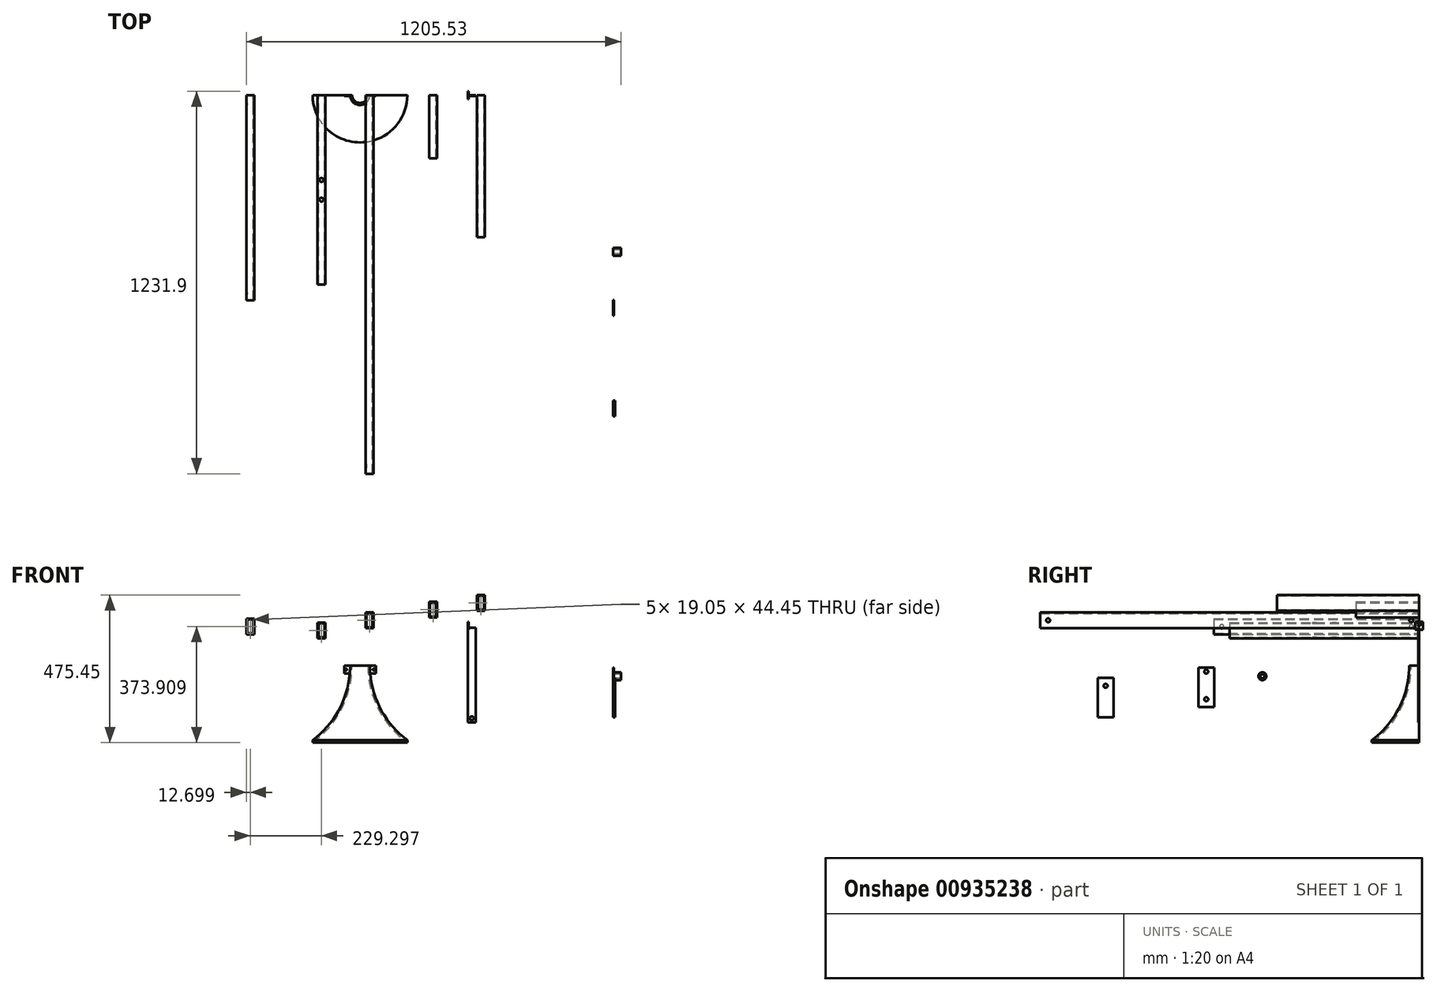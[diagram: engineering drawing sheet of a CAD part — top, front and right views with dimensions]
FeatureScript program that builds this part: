
annotation { "Feature Type Name" : "Feature", "Feature Type Description" : "" }
export const myFeature = defineFeature(function(context is Context, id is Id, definition is map)
    precondition{}
    {
        {
            var Q0;
            Q0=qCreatedBy(makeId("Front.planeOp"),FACE);
            var sketch = newSketch(context, id + "F0", { "sketchPlane" : qUnion([Q0])});
            skLineSegment(sketch, "E0.bottom", {"start": v(-947.66, 282.46) * mm, "end": v(-928.6, 282.46) * mm});
            skLineSegment(sketch, "E0.top", {"start": v(-947.66, 238) * mm, "end": v(-928.6, 238) * mm});
            skLineSegment(sketch, "E0.left", {"start": v(-947.66, 282.46) * mm, "end": v(-947.66, 238) * mm});
            skLineSegment(sketch, "E0.right", {"start": v(-928.6, 282.46) * mm, "end": v(-928.6, 238) * mm});
            skLineSegment(sketch, "E1.0", {"start": v(-950.83, 285.63) * mm, "end": v(-950.83, 234.83) * mm});
            skLineSegment(sketch, "E1.1", {"start": v(-950.83, 285.63) * mm, "end": v(-925.43, 285.63) * mm});
            skLineSegment(sketch, "E1.2", {"start": v(-925.43, 285.63) * mm, "end": v(-925.43, 234.83) * mm});
            skLineSegment(sketch, "E1.3", {"start": v(-950.83, 234.83) * mm, "end": v(-925.43, 234.83) * mm});
            skSolve(sketch);
        }
        {
            var Q0;
            Q0 = qSketchRegion(id + "F0", true);
            extrude(context, id + "F1", {"entities" : qUnion([Q0]), "depth" : 609.6 * mm, "offsetDistance" : 25.4 * mm});
        }
        {
            var Q0;
            Q0=qCreatedBy(makeId("Front.planeOp"),FACE);
            var sketch = newSketch(context, id + "F2", { "sketchPlane" : qUnion([Q0])});
            skLineSegment(sketch, "E2.bottom", {"start": v(-1176.96, 295.25) * mm, "end": v(-1157.9, 295.25) * mm});
            skLineSegment(sketch, "E2.top", {"start": v(-1176.96, 250.8) * mm, "end": v(-1157.9, 250.8) * mm});
            skLineSegment(sketch, "E2.left", {"start": v(-1176.96, 295.25) * mm, "end": v(-1176.96, 250.8) * mm});
            skLineSegment(sketch, "E2.right", {"start": v(-1157.9, 295.25) * mm, "end": v(-1157.9, 250.8) * mm});
            skLineSegment(sketch, "E3.0", {"start": v(-1180.13, 298.43) * mm, "end": v(-1180.13, 247.63) * mm});
            skLineSegment(sketch, "E3.1", {"start": v(-1180.13, 298.43) * mm, "end": v(-1154.73, 298.43) * mm});
            skLineSegment(sketch, "E3.2", {"start": v(-1154.73, 298.43) * mm, "end": v(-1154.73, 247.63) * mm});
            skLineSegment(sketch, "E3.3", {"start": v(-1180.13, 247.63) * mm, "end": v(-1154.73, 247.63) * mm});
            skSolve(sketch);
        }
        {
            var Q0;
            Q0=makeQuery(id+"F2.imprint","IMPRINT",FACE,{"disambiguationData":[TD([[makeQuery(id+"F2.imprint","IMPRINT",EDGE,{"derivedFrom":sQuery(id+"F2.wireOp",EDGE,"E2.bottom")}),1.0]])]});
            var Q1;
            Q1 = qConstructionFilter(qBodyType(qCreatedBy(id + "F2" ,EDGE), BodyType.WIRE), ConstructionObject.NO);
            extrude(context, id + "F3", {"entities" : qUnion([Q0]), "surfaceEntities" : qUnion([Q1]), "depth" : 660.4 * mm, "offsetDistance" : 25.4 * mm});
        }
        {
            var Q0;
            Q0=qCreatedBy(makeId("Front.planeOp"),FACE);
            var sketch = newSketch(context, id + "F4", { "sketchPlane" : qUnion([Q0])});
            skLineSegment(sketch, "E4.bottom", {"start": v(-792.92, 315.07) * mm, "end": v(-773.87, 315.07) * mm});
            skLineSegment(sketch, "E4.top", {"start": v(-792.92, 270.62) * mm, "end": v(-773.87, 270.62) * mm});
            skLineSegment(sketch, "E4.left", {"start": v(-792.92, 315.07) * mm, "end": v(-792.92, 270.62) * mm});
            skLineSegment(sketch, "E4.right", {"start": v(-773.87, 315.07) * mm, "end": v(-773.87, 270.62) * mm});
            skLineSegment(sketch, "E5.0", {"start": v(-796.1, 318.24) * mm, "end": v(-796.1, 267.44) * mm});
            skLineSegment(sketch, "E5.1", {"start": v(-796.1, 318.24) * mm, "end": v(-770.7, 318.24) * mm});
            skLineSegment(sketch, "E5.2", {"start": v(-770.7, 318.24) * mm, "end": v(-770.7, 267.44) * mm});
            skLineSegment(sketch, "E5.3", {"start": v(-796.1, 267.44) * mm, "end": v(-770.7, 267.44) * mm});
            skSolve(sketch);
        }
        {
            var Q0;
            Q0 = qSketchRegion(id + "F4", true);
            extrude(context, id + "F5", {"entities" : qUnion([Q0]), "depth" : 1219.2 * mm, "offsetDistance" : 25.4 * mm});
        }
        {
            var Q0;
            Q0=makeQuery(id+"F5.opExtrude","SWEPT_FACE",FACE,{"disambiguationData":[OSD([sQuery(id+"F4.wireOp",EDGE,"E5.2")])]});
            var sketch = newSketch(context, id + "F6", { "sketchPlane" : qUnion([Q0])});
            skCircle(sketch, "E6", {"center": v(-1193.8, 292.84) * mm, "radius": 6.35 * mm});
            skPoint(sketch, "E6.centerSnap0", {"position": v(-1219.2, 292.84) * mm});
            skCircle(sketch, "E7", {"center": v(-25.4, 292.84) * mm, "radius": 6.35 * mm});
            skPoint(sketch, "E7.centerSnap0", {"position": v(0, 292.84) * mm});
            skSolve(sketch);
        }
        {
            var Q0;
            Q0 = qSketchRegion(id + "F6", true);
            extrude(context, id + "F7", {"entities" : qUnion([Q0]), "operationType" : NewBodyOperationType.REMOVE, "oppositeDirection" : true, "depth" : 50.8 * mm, "offsetDistance" : 25.4 * mm});
        }
        {
            var Q0;
            Q0=qCreatedBy(makeId("Right.planeOp"),FACE);
            var sketch = newSketch(context, id + "F8", { "sketchPlane" : qUnion([Q0])});
            skLineSegment(sketch, "E8.bottom", {"start": v(-1034.2, 107.22) * mm, "end": v(-983.4, 107.22) * mm});
            skLineSegment(sketch, "E8.top", {"start": v(-1034.2, -19.78) * mm, "end": v(-983.4, -19.78) * mm});
            skLineSegment(sketch, "E8.left", {"start": v(-1034.2, 107.22) * mm, "end": v(-1034.2, -19.78) * mm});
            skLineSegment(sketch, "E8.right", {"start": v(-983.4, 107.22) * mm, "end": v(-983.4, -19.78) * mm});
            skCircle(sketch, "E9", {"center": v(-1008.8, 81.82) * mm, "radius": 6.35 * mm});
            skPoint(sketch, "E9.centerSnap0", {"position": v(-1008.8, 107.22) * mm});
            skSolve(sketch);
        }
        {
            var Q0;
            Q0=makeQuery(id+"F8.imprint","IMPRINT",FACE,{"disambiguationData":[TD([[makeQuery(id+"F8.imprint","IMPRINT",EDGE,{"derivedFrom":sQuery(id+"F8.wireOp",EDGE,"E8.bottom")}),-1.0]])]});
            extrude(context, id + "F9", {"entities" : qUnion([Q0]), "depth" : 6.35 * mm, "offsetDistance" : 25.4 * mm});
        }
        {
            var Q0;
            Q0=makeQuery(id+"F1.opExtrude","SWEPT_FACE",FACE,{"disambiguationData":[OSD([sQuery(id+"F0.wireOp",EDGE,"E1.1")])]});
            var sketch = newSketch(context, id + "F10", { "sketchPlane" : qUnion([Q0])});
            skCircle(sketch, "E10", {"center": v(-938.13, -273.05) * mm, "radius": 6.35 * mm});
            skPoint(sketch, "E10.centerSnap0", {"position": v(-938.13, 0) * mm});
            skCircle(sketch, "E11", {"center": v(-938.13, -336.55) * mm, "radius": 6.35 * mm});
            skSolve(sketch);
        }
        {
            var Q0;
            Q0 = qSketchRegion(id + "F10", true);
            extrude(context, id + "F11", {"entities" : qUnion([Q0]), "operationType" : NewBodyOperationType.REMOVE, "oppositeDirection" : true, "depth" : 50.8 * mm, "offsetDistance" : 25.4 * mm});
        }
        {
            var Q0;
            Q0=qCreatedBy(makeId("Front.planeOp"),FACE);
            var sketch = newSketch(context, id + "F12", { "sketchPlane" : qUnion([Q0])});
            skLineSegment(sketch, "E12.bottom", {"start": v(-588.77, 349) * mm, "end": v(-569.72, 349) * mm});
            skLineSegment(sketch, "E12.top", {"start": v(-588.77, 304.56) * mm, "end": v(-569.72, 304.56) * mm});
            skLineSegment(sketch, "E12.left", {"start": v(-588.77, 349) * mm, "end": v(-588.77, 304.56) * mm});
            skLineSegment(sketch, "E12.right", {"start": v(-569.72, 349) * mm, "end": v(-569.72, 304.56) * mm});
            skLineSegment(sketch, "E13.0", {"start": v(-591.95, 352.18) * mm, "end": v(-591.95, 301.38) * mm});
            skLineSegment(sketch, "E13.1", {"start": v(-591.95, 352.18) * mm, "end": v(-566.55, 352.18) * mm});
            skLineSegment(sketch, "E13.2", {"start": v(-566.55, 352.18) * mm, "end": v(-566.55, 301.38) * mm});
            skLineSegment(sketch, "E13.3", {"start": v(-591.95, 301.38) * mm, "end": v(-566.55, 301.38) * mm});
            skSolve(sketch);
        }
        {
            var Q0;
            Q0=makeQuery(id+"F12.imprint","IMPRINT",FACE,{"disambiguationData":[TD([[makeQuery(id+"F12.imprint","IMPRINT",EDGE,{"derivedFrom":sQuery(id+"F12.wireOp",EDGE,"E12.bottom")}),1.0]])]});
            var Q1;
            Q1 = qConstructionFilter(qBodyType(qCreatedBy(id + "F12" ,EDGE), BodyType.WIRE), ConstructionObject.NO);
            extrude(context, id + "F13", {"entities" : qUnion([Q0]), "surfaceEntities" : qUnion([Q1]), "depth" : 203.2 * mm, "offsetDistance" : 25.4 * mm});
        }
        {
            var Q0;
            Q0=qCreatedBy(makeId("Front.planeOp"),FACE);
            var sketch = newSketch(context, id + "F14", { "sketchPlane" : qUnion([Q0])});
            skLineSegment(sketch, "E14.bottom", {"start": v(-434.38, 371.4) * mm, "end": v(-415.33, 371.4) * mm});
            skLineSegment(sketch, "E14.top", {"start": v(-434.38, 326.95) * mm, "end": v(-415.33, 326.95) * mm});
            skLineSegment(sketch, "E14.left", {"start": v(-434.38, 371.4) * mm, "end": v(-434.38, 326.95) * mm});
            skLineSegment(sketch, "E14.right", {"start": v(-415.33, 371.4) * mm, "end": v(-415.33, 326.95) * mm});
            skLineSegment(sketch, "E15.0", {"start": v(-437.55, 374.57) * mm, "end": v(-437.55, 323.77) * mm});
            skLineSegment(sketch, "E15.1", {"start": v(-437.55, 374.57) * mm, "end": v(-412.15, 374.57) * mm});
            skLineSegment(sketch, "E15.2", {"start": v(-412.15, 374.57) * mm, "end": v(-412.15, 323.77) * mm});
            skLineSegment(sketch, "E15.3", {"start": v(-437.55, 323.77) * mm, "end": v(-412.15, 323.77) * mm});
            skSolve(sketch);
        }
        {
            var Q0;
            Q0=makeQuery(id+"F14.imprint","IMPRINT",FACE,{"disambiguationData":[TD([[makeQuery(id+"F14.imprint","IMPRINT",EDGE,{"derivedFrom":sQuery(id+"F14.wireOp",EDGE,"E14.bottom")}),1.0]])]});
            var Q1;
            Q1 = qConstructionFilter(qBodyType(qCreatedBy(id + "F14" ,EDGE), BodyType.WIRE), ConstructionObject.NO);
            extrude(context, id + "F15", {"entities" : qUnion([Q0]), "surfaceEntities" : qUnion([Q1]), "depth" : 457.2 * mm, "offsetDistance" : 25.4 * mm});
        }
        {
            var Q0;
            Q0=makeQuery(id+"F3.opExtrude","SWEPT_FACE",FACE,{"disambiguationData":[OSD([sQuery(id+"F2.wireOp",EDGE,"E3.0")])]});
            var sketch = newSketch(context, id + "F16", { "sketchPlane" : qUnion([Q0])});
            skCircle(sketch, "E16", {"center": v(635, 273.03) * mm, "radius": 6.35 * mm});
            skPoint(sketch, "E16.centerSnap0", {"position": v(660.4, 273.03) * mm});
            skCircle(sketch, "E17", {"center": v(25.4, 273.03) * mm, "radius": 6.35 * mm});
            skPoint(sketch, "E17.centerSnap0", {"position": v(0, 273.03) * mm});
            skSolve(sketch);
        }
        {
            var Q0;
            Q0 = qSketchRegion(id + "F16", true);
            extrude(context, id + "F17", {"entities" : qUnion([Q0]), "operationType" : NewBodyOperationType.REMOVE, "oppositeDirection" : true, "depth" : 38.1 * mm, "offsetDistance" : 25.4 * mm});
        }
        {
            var Q0;
            Q0=qCreatedBy(makeId("Right.planeOp"),FACE);
            var sketch = newSketch(context, id + "F18", { "sketchPlane" : qUnion([Q0])});
            skLineSegment(sketch, "E18.bottom", {"start": v(-710.31, 140.19) * mm, "end": v(-659.51, 140.19) * mm});
            skLineSegment(sketch, "E18.top", {"start": v(-710.31, 13.19) * mm, "end": v(-659.51, 13.19) * mm});
            skLineSegment(sketch, "E18.left", {"start": v(-710.31, 140.19) * mm, "end": v(-710.31, 13.19) * mm});
            skLineSegment(sketch, "E18.right", {"start": v(-659.51, 140.19) * mm, "end": v(-659.51, 13.19) * mm});
            skCircle(sketch, "E19", {"center": v(-684.91, 127.49) * mm, "radius": 6.35 * mm});
            skCircle(sketch, "E20", {"center": v(-684.91, 38.59) * mm, "radius": 6.35 * mm});
            skPoint(sketch, "E20.centerSnap0", {"position": v(-684.91, 13.19) * mm});
            skSolve(sketch);
        }
        {
            var Q0;
            Q0 = qSketchRegion(id + "F18", true);
            extrude(context, id + "F19", {"entities" : qUnion([Q0]), "depth" : 3.17 * mm, "offsetDistance" : 25.4 * mm});
        }
        {
            var Q0;
            Q0=qCreatedBy(makeId("Right.planeOp"),FACE);
            var sketch = newSketch(context, id + "F20", { "sketchPlane" : qUnion([Q0])});
            skCircle(sketch, "E21", {"center": v(-504.4, 112.85) * mm, "radius": 6.35 * mm});
            skCircle(sketch, "E22", {"center": v(-504.4, 112.85) * mm, "radius": 12.7 * mm});
            skSolve(sketch);
        }
        {
            var Q0;
            Q0 = qSketchRegion(id + "F20", true);
            extrude(context, id + "F21", {"entities" : qUnion([Q0]), "depth" : 25.4 * mm, "offsetDistance" : 25.4 * mm});
        }
        {
            var Q0;
            Q0=qCreatedBy(makeId("Front.planeOp"),FACE);
            var sketch = newSketch(context, id + "F22", { "sketchPlane" : qUnion([Q0])});
            skLineSegment(sketch, "E23", {"start": v(-814.2, 205.13) * mm, "end": v(-814.2, 146.68) * mm, "construction": true});
            skLineSegment(sketch, "E24.bottom", {"start": v(-814.2, 146.68) * mm, "end": v(-788.8, 146.7) * mm, "construction": true});
            skLineSegment(sketch, "E24.right", {"start": v(-661.8, 146.74) * mm, "end": v(-661.8, -90.7) * mm, "construction": true});
            skArc(sketch, "E25", {"start": v(-788.8, 146.7) * mm, "mid": v(-755.19, 7.57) * mm, "end": v(-661.8, -100.88) * mm});
            skArc(sketch, "E26.0", {"start": v(-782.44, 146.7) * mm, "mid": v(-750.58, 12.51) * mm, "end": v(-661.8, -93.01) * mm});
            skLineSegment(sketch, "E27.trimOffspring", {"start": v(-778.56, 146.7) * mm, "end": v(-661.8, 146.74) * mm, "construction": true});
            skLineSegment(sketch, "E28", {"start": v(-788.8, 146.7) * mm, "end": v(-782.44, 146.7) * mm});
            skLineSegment(sketch, "E29", {"start": v(-661.8, -100.88) * mm, "end": v(-661.8, -93.01) * mm});
            skLineSegment(sketch, "E30.trimOffspring", {"start": v(-661.8, -93.01) * mm, "end": v(-661.8, -100.88) * mm, "construction": true});
            skSolve(sketch);
        }
        {
            var Q0;
            Q0 = qSketchRegion(id + "F22", true);
            var Q1;
            Q1=sQuery(id+"F22.wireOp",EDGE,"E23");
            revolve(context, id + "F23", {"surfaceOperationType" : NewSurfaceOperationType.NEW, "entities" : qUnion([Q0]), "axis" : qUnion([Q1]), "revolveType" : RevolveType.ONE_DIRECTION, "angle" : 180 * degree});
        }
        {
            var Q0;
            Q0=makeQuery(id+"F23.opRevolve","CAP_FACE",FACE,{"disambiguationData":[OSD([sQuery(id+"F22.wireOp",EDGE,"E25"),sQuery(id+"F22.wireOp",EDGE,"E26.0"),sQuery(id+"F22.wireOp",EDGE,"E28"),sQuery(id+"F22.wireOp",EDGE,"E29")])],"isStart":false});
            var sketch = newSketch(context, id + "F24", { "sketchPlane" : qUnion([Q0])});
            skLineSegment(sketch, "E31.left", {"start": v(865, 146.7) * mm, "end": v(865, 121.3) * mm});
            skLineSegment(sketch, "E31.right", {"start": v(763.4, 146.7) * mm, "end": v(763.4, 121.3) * mm});
            skArc(sketch, "E32.0.3", {"start": v(781.36, 121.3) * mm, "mid": v(782.17, 133.98) * mm, "end": v(782.44, 146.7) * mm});
            skPoint(sketch, "E32.0.2.end.orphan", {"position": v(966.6, -93.01) * mm});
            skPoint(sketch, "E32.0.2.start.orphan", {"position": v(661.8, -93.01) * mm});
            skCircle(sketch, "E33", {"center": v(769.74, 134) * mm, "radius": 2.95 * mm});
            skCircle(sketch, "E34", {"center": v(858.64, 134) * mm, "radius": 2.63 * mm});
            skArc(sketch, "E35.0", {"start": v(839.6, 146.7) * mm, "mid": v(839.86, 133.98) * mm, "end": v(840.65, 121.3) * mm});
            skArc(sketch, "E36.0", {"start": v(788.8, 146.7) * mm, "mid": v(755.19, 7.57) * mm, "end": v(661.8, -100.88) * mm});
            skPoint(sketch, "E37.start.orphan", {"position": v(845.94, 146.7) * mm});
            skLineSegment(sketch, "E38", {"start": v(839.6, 146.7) * mm, "end": v(865, 146.7) * mm});
            skLineSegment(sketch, "E39", {"start": v(865, 121.3) * mm, "end": v(840.65, 121.3) * mm});
            skPoint(sketch, "E40.orphan", {"position": v(966.6, -100.88) * mm});
            skLineSegment(sketch, "E41", {"start": v(788.8, 146.7) * mm, "end": v(763.4, 146.7) * mm});
            skLineSegment(sketch, "E42", {"start": v(763.4, 121.3) * mm, "end": v(787.73, 121.3) * mm});
            skSolve(sketch);
        }
        {
            var Q0;
            Q0 = qSketchRegion(id + "F24", true);
            extrude(context, id + "F25", {"entities" : qUnion([Q0]), "operationType" : NewBodyOperationType.ADD, "oppositeDirection" : true, "depth" : 3.17 * mm, "offsetDistance" : 25.4 * mm});
        }
        {
            var Q0;
            Q0=qCreatedBy(makeId("Front.planeOp"),FACE);
            var sketch = newSketch(context, id + "F26", { "sketchPlane" : qUnion([Q0])});
            skLineSegment(sketch, "E43.bottom", {"start": v(-467.1, 269.5) * mm, "end": v(-441.7, 269.5) * mm});
            skLineSegment(sketch, "E43.top", {"start": v(-467.1, -35.3) * mm, "end": v(-441.7, -35.3) * mm});
            skLineSegment(sketch, "E43.left", {"start": v(-467.1, 269.5) * mm, "end": v(-467.1, -35.3) * mm});
            skLineSegment(sketch, "E43.right", {"start": v(-441.7, 269.5) * mm, "end": v(-441.7, -35.3) * mm});
            skCircle(sketch, "E44", {"center": v(-454.4, -22.6) * mm, "radius": 6.35 * mm});
            skPoint(sketch, "E44.centerSnap0", {"position": v(-454.4, -35.3) * mm});
            skSolve(sketch);
        }
        {
            var Q0;
            Q0 = qSketchRegion(id + "F26", true);
            extrude(context, id + "F27", {"entities" : qUnion([Q0]), "depth" : 3.17 * mm, "offsetDistance" : 25.4 * mm});
        }
        {
            var Q0;
            Q0=makeQuery(id+"F27.opExtrude","CAP_FACE",FACE,{"disambiguationData":[OSD([sQuery(id+"F26.wireOp",EDGE,"E43.bottom"),sQuery(id+"F26.wireOp",EDGE,"E43.top"),sQuery(id+"F26.wireOp",EDGE,"E43.left"),sQuery(id+"F26.wireOp",EDGE,"E43.right"),sQuery(id+"F26.wireOp",EDGE,"E44")])],"isStart":true});
            var sketch = newSketch(context, id + "F28", { "sketchPlane" : qUnion([Q0])});
            skLineSegment(sketch, "E45.top", {"start": v(467.1, 288.55) * mm, "end": v(463.93, 288.55) * mm});
            skLineSegment(sketch, "E46.top", {"start": v(463.93, 263.15) * mm, "end": v(467.1, 263.15) * mm});
            skLineSegment(sketch, "E47", {"start": v(467.1, 288.55) * mm, "end": v(467.1, 263.15) * mm});
            skLineSegment(sketch, "E48", {"start": v(463.93, 288.55) * mm, "end": v(463.93, 263.15) * mm});
            skSolve(sketch);
        }
        {
            var Q0;
            Q0 = qSketchRegion(id + "F28", true);
            extrude(context, id + "F29", {"entities" : qUnion([Q0]), "operationType" : NewBodyOperationType.ADD, "endBound" : BoundingType.SYMMETRIC, "depth" : 25.4 * mm, "offsetDistance" : 25.4 * mm});
        }
        {
            var Q0;
            Q0=makeQuery(id+"F29.opExtrude","SWEPT_FACE",FACE,{"disambiguationData":[OSD([sQuery(id+"F28.wireOp",EDGE,"E48")])]});
            var sketch = newSketch(context, id + "F30", { "sketchPlane" : qUnion([Q0])});
            skCircle(sketch, "E49", {"center": v(0, 279.02) * mm, "radius": 4.65 * mm});
            skSolve(sketch);
        }
        {
            var Q0;
            Q0 = qSketchRegion(id + "F30", true);
            extrude(context, id + "F31", {"entities" : qUnion([Q0]), "operationType" : NewBodyOperationType.REMOVE, "oppositeDirection" : true, "depth" : 25.4 * mm, "offsetDistance" : 25.4 * mm});
        }
    });
